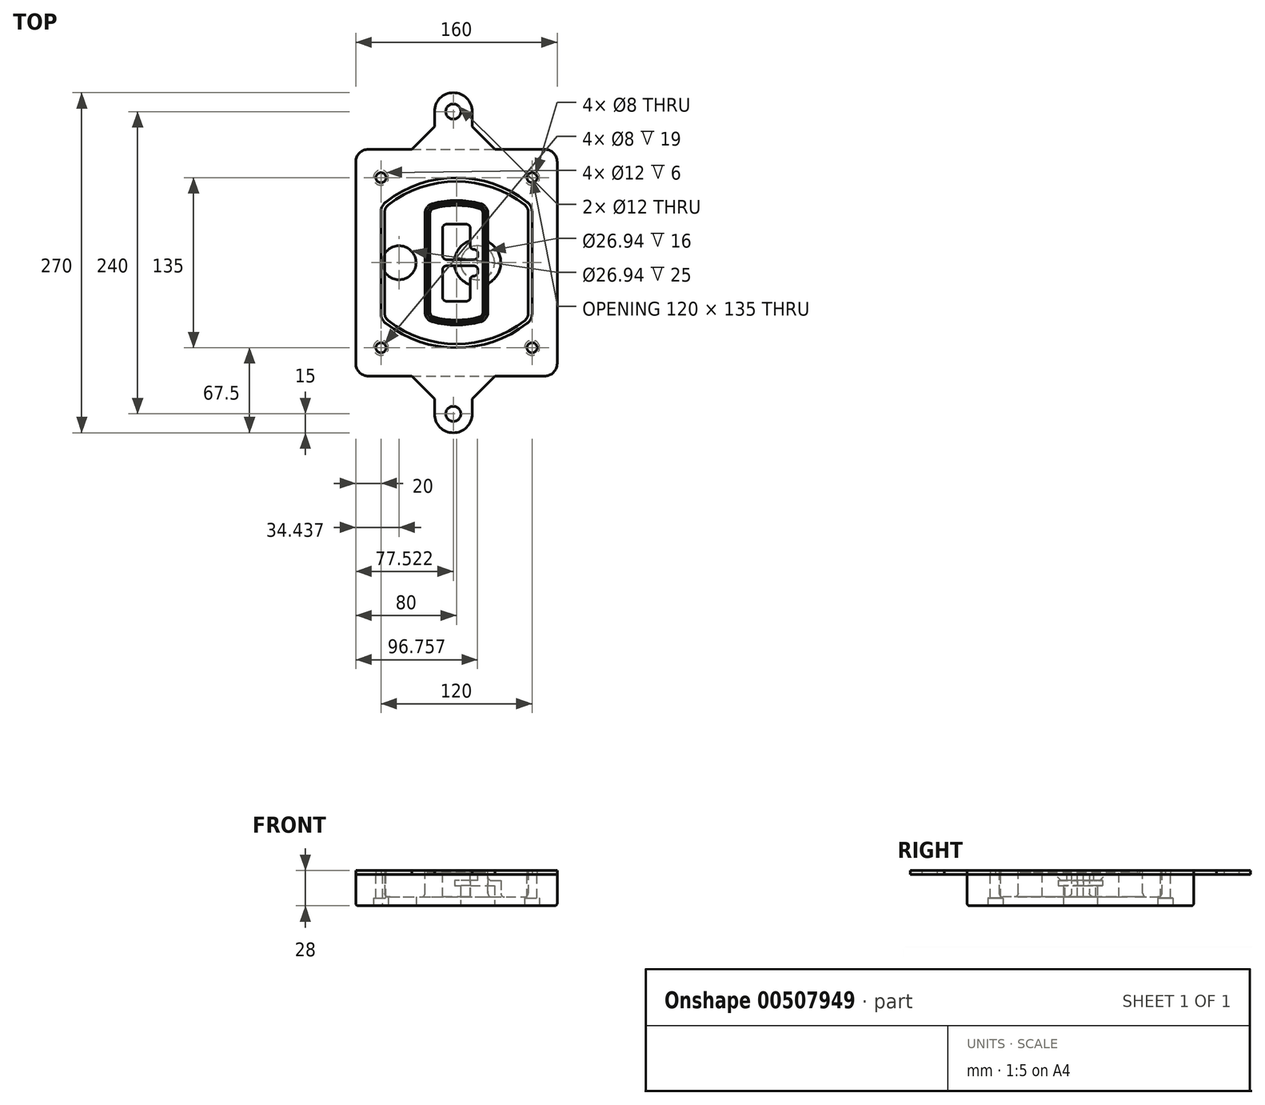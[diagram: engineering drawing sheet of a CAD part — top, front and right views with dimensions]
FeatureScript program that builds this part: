
annotation { "Feature Type Name" : "Feature", "Feature Type Description" : "" }
export const myFeature = defineFeature(function(context is Context, id is Id, definition is map)
    precondition{}
    {
        {
            var Q0;
            Q0=qCreatedBy(makeId("Top.planeOp"),FACE);
            var sketch = newSketch(context, id + "F0", { "sketchPlane" : qUnion([Q0])});
            skPoint(sketch, "E0.rect.middle", {"position": v(0, 0) * mm});
            skLineSegment(sketch, "E1.bottom", {"start": v(-70, -90) * mm, "end": v(70, -90) * mm});
            skLineSegment(sketch, "E1.top", {"start": v(-70, 90) * mm, "end": v(70, 90) * mm});
            skLineSegment(sketch, "E1.left", {"start": v(-80, -80) * mm, "end": v(-80, 80) * mm});
            skLineSegment(sketch, "E1.right", {"start": v(80, -80) * mm, "end": v(80, 80) * mm});
            skLineSegment(sketch, "E2", {"start": v(-80, 90) * mm, "end": v(80, -90) * mm, "construction": true});
            skLineSegment(sketch, "E3", {"start": v(80, 90) * mm, "end": v(-80, -90) * mm, "construction": true});
            skCircle(sketch, "E4", {"center": v(-60, 67.5) * mm, "radius": 4 * mm});
            skCircle(sketch, "E5", {"center": v(60, 67.5) * mm, "radius": 4 * mm});
            skCircle(sketch, "E6", {"center": v(60, -67.5) * mm, "radius": 4 * mm});
            skCircle(sketch, "E7", {"center": v(-60, -67.5) * mm, "radius": 4 * mm});
            skLineSegment(sketch, "E8", {"start": v(-60, 67.5) * mm, "end": v(60, 67.5) * mm, "construction": true});
            skLineSegment(sketch, "E9", {"start": v(60, 67.5) * mm, "end": v(60, -67.5) * mm, "construction": true});
            skLineSegment(sketch, "E10", {"start": v(60, -67.5) * mm, "end": v(-60, -67.5) * mm, "construction": true});
            skLineSegment(sketch, "E11", {"start": v(-60, -67.5) * mm, "end": v(-60, 67.5) * mm, "construction": true});
            skLineSegment(sketch, "E12", {"start": v(-60, 40.3) * mm, "end": v(-60, -40.3) * mm});
            skLineSegment(sketch, "E13", {"start": v(60, 40.3) * mm, "end": v(60, -40.3) * mm});
            skArc(sketch, "E14", {"start": v(56.15, 48.18) * mm, "mid": v(0, 67.5) * mm, "end": v(-56.15, 48.18) * mm});
            skArc(sketch, "E15", {"start": v(-56.15, -48.18) * mm, "mid": v(0, -67.5) * mm, "end": v(56.15, -48.18) * mm});
            skLineSegment(sketch, "E16", {"start": v(-60, 0) * mm, "end": v(60, 0) * mm, "construction": true});
            skPoint(sketch, "E17.visualSharp", {"position": v(-60, -45) * mm});
            skArc(sketch, "E17.filletArc", {"start": v(-60, -40.3) * mm, "mid": v(-58.99, -44.68) * mm, "end": v(-56.15, -48.18) * mm});
            skPoint(sketch, "E18.visualSharp", {"position": v(-60, 45) * mm});
            skArc(sketch, "E18.filletArc", {"start": v(-56.15, 48.18) * mm, "mid": v(-58.99, 44.68) * mm, "end": v(-60, 40.3) * mm});
            skPoint(sketch, "E19.visualSharp", {"position": v(60, 45) * mm});
            skArc(sketch, "E19.filletArc", {"start": v(60, 40.3) * mm, "mid": v(58.99, 44.68) * mm, "end": v(56.15, 48.18) * mm});
            skPoint(sketch, "E20.visualSharp", {"position": v(60, -45) * mm});
            skArc(sketch, "E20.filletArc", {"start": v(56.15, -48.18) * mm, "mid": v(58.99, -44.68) * mm, "end": v(60, -40.3) * mm});
            skPoint(sketch, "E21.visualSharp", {"position": v(-80, 90) * mm});
            skArc(sketch, "E21.filletArc", {"start": v(-70, 90) * mm, "mid": v(-77.07, 87.07) * mm, "end": v(-80, 80) * mm});
            skPoint(sketch, "E22.visualSharp", {"position": v(80, 90) * mm});
            skArc(sketch, "E22.filletArc", {"start": v(80, 80) * mm, "mid": v(77.07, 87.07) * mm, "end": v(70, 90) * mm});
            skPoint(sketch, "E23.visualSharp", {"position": v(80, -90) * mm});
            skArc(sketch, "E23.filletArc", {"start": v(70, -90) * mm, "mid": v(77.07, -87.07) * mm, "end": v(80, -80) * mm});
            skPoint(sketch, "E24.visualSharp", {"position": v(-80, -90) * mm});
            skArc(sketch, "E24.filletArc", {"start": v(-80, -80) * mm, "mid": v(-77.07, -87.07) * mm, "end": v(-70, -90) * mm});
            skArc(sketch, "E25.0", {"start": v(57, 40.3) * mm, "mid": v(56.3, 43.36) * mm, "end": v(54.3, 45.81) * mm});
            skLineSegment(sketch, "E25.1", {"start": v(57, 40.3) * mm, "end": v(57, -40.3) * mm});
            skArc(sketch, "E25.2", {"start": v(54.3, -45.81) * mm, "mid": v(56.3, -43.36) * mm, "end": v(57, -40.3) * mm});
            skArc(sketch, "E25.3", {"start": v(-54.3, -45.81) * mm, "mid": v(0, -64.5) * mm, "end": v(54.3, -45.81) * mm});
            skArc(sketch, "E25.4", {"start": v(-57, -40.3) * mm, "mid": v(-56.3, -43.36) * mm, "end": v(-54.3, -45.81) * mm});
            skArc(sketch, "E25.5", {"start": v(54.3, 45.81) * mm, "mid": v(0, 64.5) * mm, "end": v(-54.3, 45.81) * mm});
            skLineSegment(sketch, "E25.6", {"start": v(-57, 40.3) * mm, "end": v(-57, -40.3) * mm});
            skArc(sketch, "E25.7", {"start": v(-54.3, 45.81) * mm, "mid": v(-56.3, 43.36) * mm, "end": v(-57, 40.3) * mm});
            skArc(sketch, "E26.0", {"start": v(-58.62, 51.33) * mm, "mid": v(-62.58, 46.43) * mm, "end": v(-64, 40.3) * mm});
            skArc(sketch, "E26.1", {"start": v(58.62, 51.33) * mm, "mid": v(0, 71.5) * mm, "end": v(-58.62, 51.33) * mm});
            skArc(sketch, "E26.2", {"start": v(64, 40.3) * mm, "mid": v(62.58, 46.43) * mm, "end": v(58.62, 51.33) * mm});
            skLineSegment(sketch, "E26.3", {"start": v(64, 40.3) * mm, "end": v(64, -40.3) * mm});
            skArc(sketch, "E26.4", {"start": v(58.62, -51.33) * mm, "mid": v(62.58, -46.43) * mm, "end": v(64, -40.3) * mm});
            skLineSegment(sketch, "E26.5", {"start": v(-64, 40.3) * mm, "end": v(-64, -40.3) * mm});
            skArc(sketch, "E26.6", {"start": v(-58.62, -51.33) * mm, "mid": v(0, -71.5) * mm, "end": v(58.62, -51.33) * mm});
            skArc(sketch, "E26.7", {"start": v(-64, -40.3) * mm, "mid": v(-62.58, -46.43) * mm, "end": v(-58.62, -51.33) * mm});
            skSolve(sketch);
        }
        {
            var Q0;
            Q0=makeQuery(id+"F0.imprint","IMPRINT",FACE,{"disambiguationData":[TD([[makeQuery(id+"F0.imprint","IMPRINT",EDGE,{"derivedFrom":sQuery(id+"F0.wireOp",EDGE,"E1.bottom")}),1.0]])]});
            var Q1;
            Q1=makeQuery(id+"F0.imprint","IMPRINT",FACE,{"disambiguationData":[TD([[makeQuery(id+"F0.imprint","IMPRINT",EDGE,{"derivedFrom":sQuery(id+"F0.wireOp",EDGE,"E12")}),1.0]])]});
            var Q2;
            Q2=makeQuery(id+"F0.imprint","IMPRINT",FACE,{"disambiguationData":[TD([[makeQuery(id+"F0.imprint","IMPRINT",EDGE,{"derivedFrom":sQuery(id+"F0.wireOp",EDGE,"E25.0")}),1.0]])]});
            var Q3;
            Q3=makeQuery(id+"F0.imprint","IMPRINT",FACE,{"disambiguationData":[TD([[makeQuery(id+"F0.imprint","IMPRINT",EDGE,{"derivedFrom":sQuery(id+"F0.wireOp",EDGE,"E12")}),-1.0]])]});
            extrude(context, id + "F1", {"entities" : qUnion([Q0, Q1, Q2, Q3]), "oppositeDirection" : true, "depth" : 25 * mm});
        }
        {
            var Q0;
            Q0=makeQuery(id+"F0.imprint","IMPRINT",FACE,{"disambiguationData":[TD([[makeQuery(id+"F0.imprint","IMPRINT",EDGE,{"derivedFrom":sQuery(id+"F0.wireOp",EDGE,"E12")}),1.0]])]});
            extrude(context, id + "F2", {"entities" : qUnion([Q0]), "operationType" : NewBodyOperationType.ADD, "depth" : 3 * mm});
        }
        {
            var Q0;
            Q0=makeQuery(id+"F0.imprint","IMPRINT",FACE,{"disambiguationData":[TD([[makeQuery(id+"F0.imprint","IMPRINT",EDGE,{"derivedFrom":sQuery(id+"F0.wireOp",EDGE,"E25.0")}),1.0]])]});
            extrude(context, id + "F3", {"entities" : qUnion([Q0]), "operationType" : NewBodyOperationType.REMOVE, "oppositeDirection" : true, "depth" : 18 * mm});
        }
        {
            var Q0;
            Q0=makeQuery(id+"F2.opExtrude","CAP_FACE",FACE,{"disambiguationData":[OSD([sQuery(id+"F0.wireOp",EDGE,"E12"),sQuery(id+"F0.wireOp",EDGE,"E13"),sQuery(id+"F0.wireOp",EDGE,"E14"),sQuery(id+"F0.wireOp",EDGE,"E15"),sQuery(id+"F0.wireOp",EDGE,"E17.filletArc"),sQuery(id+"F0.wireOp",EDGE,"E18.filletArc"),sQuery(id+"F0.wireOp",EDGE,"E19.filletArc"),sQuery(id+"F0.wireOp",EDGE,"E20.filletArc"),sQuery(id+"F0.wireOp",EDGE,"E25.0"),sQuery(id+"F0.wireOp",EDGE,"E25.1"),sQuery(id+"F0.wireOp",EDGE,"E25.2"),sQuery(id+"F0.wireOp",EDGE,"E25.3"),sQuery(id+"F0.wireOp",EDGE,"E25.4"),sQuery(id+"F0.wireOp",EDGE,"E25.5"),sQuery(id+"F0.wireOp",EDGE,"E25.6"),sQuery(id+"F0.wireOp",EDGE,"E25.7")])],"isStart":false});
            var sketch = newSketch(context, id + "F4", { "sketchPlane" : qUnion([Q0])});
            skArc(sketch, "E27.0", {"start": v(-19.08, -46.97) * mm, "mid": v(0, -49.5) * mm, "end": v(19.08, -46.97) * mm});
            skArc(sketch, "E28.0", {"start": v(19.08, 46.97) * mm, "mid": v(0, 49.5) * mm, "end": v(-19.08, 46.97) * mm});
            skLineSegment(sketch, "E29", {"start": v(-25, 39.25) * mm, "end": v(-25, -39.25) * mm});
            skLineSegment(sketch, "E30", {"start": v(25, 39.25) * mm, "end": v(25, -39.25) * mm});
            skLineSegment(sketch, "E31", {"start": v(-25, 45.1) * mm, "end": v(25, 45.1) * mm, "construction": true});
            skLineSegment(sketch, "E32", {"start": v(-25, -45.1) * mm, "end": v(25, -45.1) * mm, "construction": true});
            skPoint(sketch, "E33.visualSharp", {"position": v(-25, 45.1) * mm});
            skArc(sketch, "E33.filletArc", {"start": v(-19.08, 46.97) * mm, "mid": v(-23.35, 44.11) * mm, "end": v(-25, 39.25) * mm});
            skPoint(sketch, "E34.visualSharp", {"position": v(25, 45.1) * mm});
            skArc(sketch, "E34.filletArc", {"start": v(25, 39.25) * mm, "mid": v(23.35, 44.11) * mm, "end": v(19.08, 46.97) * mm});
            skPoint(sketch, "E35.visualSharp", {"position": v(25, -45.1) * mm});
            skArc(sketch, "E35.filletArc", {"start": v(19.08, -46.97) * mm, "mid": v(23.35, -44.11) * mm, "end": v(25, -39.25) * mm});
            skPoint(sketch, "E36.visualSharp", {"position": v(-25, -45.1) * mm});
            skArc(sketch, "E36.filletArc", {"start": v(-25, -39.25) * mm, "mid": v(-23.35, -44.11) * mm, "end": v(-19.08, -46.97) * mm});
            skArc(sketch, "E37.0", {"start": v(54.3, 45.81) * mm, "mid": v(0, 64.5) * mm, "end": v(-54.3, 45.81) * mm});
            skArc(sketch, "E37.1", {"start": v(-54.3, 45.81) * mm, "mid": v(-56.3, 43.36) * mm, "end": v(-57, 40.3) * mm});
            skLineSegment(sketch, "E37.2", {"start": v(-57, 40.3) * mm, "end": v(-57, -40.3) * mm});
            skArc(sketch, "E37.3", {"start": v(-57, -40.3) * mm, "mid": v(-56.3, -43.36) * mm, "end": v(-54.3, -45.81) * mm});
            skArc(sketch, "E37.4", {"start": v(-54.3, -45.81) * mm, "mid": v(0, -64.5) * mm, "end": v(54.3, -45.81) * mm});
            skArc(sketch, "E37.5", {"start": v(54.3, -45.81) * mm, "mid": v(56.3, -43.36) * mm, "end": v(57, -40.3) * mm});
            skLineSegment(sketch, "E37.6", {"start": v(57, 40.3) * mm, "end": v(57, -40.3) * mm});
            skArc(sketch, "E37.7", {"start": v(57, 40.3) * mm, "mid": v(56.3, 43.36) * mm, "end": v(54.3, 45.81) * mm});
            skLineSegment(sketch, "E38.0", {"start": v(23, 39.25) * mm, "end": v(23, -39.25) * mm});
            skArc(sketch, "E38.1", {"start": v(18.56, -45.04) * mm, "mid": v(21.76, -42.9) * mm, "end": v(23, -39.25) * mm});
            skArc(sketch, "E38.2", {"start": v(-18.56, -45.04) * mm, "mid": v(0, -47.5) * mm, "end": v(18.56, -45.04) * mm});
            skArc(sketch, "E38.3", {"start": v(-23, -39.25) * mm, "mid": v(-21.76, -42.9) * mm, "end": v(-18.56, -45.04) * mm});
            skLineSegment(sketch, "E38.4", {"start": v(-23, 39.25) * mm, "end": v(-23, -39.25) * mm});
            skArc(sketch, "E38.5", {"start": v(23, 39.25) * mm, "mid": v(21.76, 42.9) * mm, "end": v(18.56, 45.04) * mm});
            skArc(sketch, "E38.6", {"start": v(-18.56, 45.04) * mm, "mid": v(-21.76, 42.9) * mm, "end": v(-23, 39.25) * mm});
            skArc(sketch, "E38.7", {"start": v(18.56, 45.04) * mm, "mid": v(0, 47.5) * mm, "end": v(-18.56, 45.04) * mm});
            skArc(sketch, "E39.0", {"start": v(21, 39.25) * mm, "mid": v(20.18, 41.68) * mm, "end": v(18.04, 43.1) * mm});
            skLineSegment(sketch, "E39.1", {"start": v(21, 39.25) * mm, "end": v(21, -39.25) * mm});
            skArc(sketch, "E39.2", {"start": v(18.04, -43.1) * mm, "mid": v(20.18, -41.68) * mm, "end": v(21, -39.25) * mm});
            skArc(sketch, "E39.3", {"start": v(-18.04, -43.1) * mm, "mid": v(0, -45.5) * mm, "end": v(18.04, -43.1) * mm});
            skArc(sketch, "E39.4", {"start": v(-21, -39.25) * mm, "mid": v(-20.18, -41.68) * mm, "end": v(-18.04, -43.1) * mm});
            skArc(sketch, "E39.5", {"start": v(18.04, 43.1) * mm, "mid": v(0, 45.5) * mm, "end": v(-18.04, 43.1) * mm});
            skLineSegment(sketch, "E39.6", {"start": v(-21, 39.25) * mm, "end": v(-21, -39.25) * mm});
            skArc(sketch, "E39.7", {"start": v(-18.04, 43.1) * mm, "mid": v(-20.18, 41.68) * mm, "end": v(-21, 39.25) * mm});
            skLineSegment(sketch, "E40", {"start": v(-25, 0) * mm, "end": v(25, 0) * mm, "construction": true});
            skLineSegment(sketch, "E41", {"start": v(-11, 5.5) * mm, "end": v(-11, 27.5) * mm});
            skLineSegment(sketch, "E42", {"start": v(-8, 30.5) * mm, "end": v(8, 30.5) * mm});
            skLineSegment(sketch, "E43", {"start": v(11, 27.5) * mm, "end": v(11, 13.5) * mm});
            skLineSegment(sketch, "E44", {"start": v(14, 10.5) * mm, "end": v(14, 10.5) * mm});
            skLineSegment(sketch, "E45", {"start": v(17, 7.5) * mm, "end": v(17, 5.5) * mm});
            skLineSegment(sketch, "E46", {"start": v(14, 2.5) * mm, "end": v(-8, 2.5) * mm});
            skPoint(sketch, "E47.visualSharp", {"position": v(-11, 30.5) * mm});
            skArc(sketch, "E47.filletArc", {"start": v(-8, 30.5) * mm, "mid": v(-10.12, 29.62) * mm, "end": v(-11, 27.5) * mm});
            skPoint(sketch, "E48.visualSharp", {"position": v(11, 30.5) * mm});
            skArc(sketch, "E48.filletArc", {"start": v(11, 27.5) * mm, "mid": v(10.12, 29.62) * mm, "end": v(8, 30.5) * mm});
            skPoint(sketch, "E49.visualSharp", {"position": v(11, 10.5) * mm});
            skArc(sketch, "E49.filletArc", {"start": v(11, 13.5) * mm, "mid": v(11.88, 11.38) * mm, "end": v(14, 10.5) * mm});
            skPoint(sketch, "E50.visualSharp", {"position": v(17, 10.5) * mm});
            skArc(sketch, "E50.filletArc", {"start": v(17, 7.5) * mm, "mid": v(16.12, 9.62) * mm, "end": v(14, 10.5) * mm});
            skPoint(sketch, "E51.visualSharp", {"position": v(17, 2.5) * mm});
            skArc(sketch, "E51.filletArc", {"start": v(14, 2.5) * mm, "mid": v(16.12, 3.38) * mm, "end": v(17, 5.5) * mm});
            skPoint(sketch, "E52.visualSharp", {"position": v(-11, 2.5) * mm});
            skArc(sketch, "E52.filletArc", {"start": v(-11, 5.5) * mm, "mid": v(-10.12, 3.38) * mm, "end": v(-8, 2.5) * mm});
            skLineSegment(sketch, "E53.0.MirrorCS", {"start": v(14, -2.5) * mm, "end": v(-8, -2.5) * mm});
            skArc(sketch, "E54.0.MirrorCS", {"start": v(-11, -5.5) * mm, "mid": v(-10.12, -3.38) * mm, "end": v(-8, -2.5) * mm});
            skLineSegment(sketch, "E55.0.MirrorCS", {"start": v(-11, -5.5) * mm, "end": v(-11, -27.5) * mm});
            skArc(sketch, "E56.0.MirrorCS", {"start": v(-8, -30.5) * mm, "mid": v(-10.12, -29.62) * mm, "end": v(-11, -27.5) * mm});
            skLineSegment(sketch, "E57.0.MirrorCS", {"start": v(-8, -30.5) * mm, "end": v(8, -30.5) * mm});
            skArc(sketch, "E58.0.MirrorCS", {"start": v(11, -27.5) * mm, "mid": v(10.12, -29.62) * mm, "end": v(8, -30.5) * mm});
            skLineSegment(sketch, "E59.0.MirrorCS", {"start": v(11, -27.5) * mm, "end": v(11, -13.5) * mm});
            skArc(sketch, "E60.0.MirrorCS", {"start": v(11, -13.5) * mm, "mid": v(11.88, -11.38) * mm, "end": v(14, -10.5) * mm});
            skArc(sketch, "E61.0.MirrorCS", {"start": v(17, -7.5) * mm, "mid": v(16.12, -9.62) * mm, "end": v(14, -10.5) * mm});
            skLineSegment(sketch, "E62.0.MirrorCS", {"start": v(17, -7.5) * mm, "end": v(17, -5.5) * mm});
            skArc(sketch, "E63.0.MirrorCS", {"start": v(14, -2.5) * mm, "mid": v(16.12, -3.38) * mm, "end": v(17, -5.5) * mm});
            skSolve(sketch);
        }
        {
            var Q0;
            Q0=makeQuery(id+"F4.imprint","IMPRINT",FACE,{"disambiguationData":[TD([[makeQuery(id+"F4.imprint","IMPRINT",EDGE,{"derivedFrom":sQuery(id+"F4.wireOp",EDGE,"E27.0")}),1.0]])]});
            var Q1;
            Q1=makeQuery(id+"F4.imprint","IMPRINT",FACE,{"disambiguationData":[TD([[makeQuery(id+"F4.imprint","IMPRINT",EDGE,{"derivedFrom":sQuery(id+"F4.wireOp",EDGE,"E38.0")}),-1.0]])]});
            var Q2;
            Q2=makeQuery(id+"F4.imprint","IMPRINT",FACE,{"disambiguationData":[TD([[makeQuery(id+"F4.imprint","IMPRINT",EDGE,{"derivedFrom":sQuery(id+"F4.wireOp",EDGE,"E39.0")}),1.0]])]});
            extrude(context, id + "F5", {"entities" : qUnion([Q0, Q1, Q2]), "operationType" : NewBodyOperationType.ADD, "endBound" : BoundingType.UP_TO_NEXT, "oppositeDirection" : true, "depth" : 25 * mm});
        }
        {
            var Q0;
            Q0=makeQuery(id+"F4.imprint","IMPRINT",FACE,{"disambiguationData":[TD([[makeQuery(id+"F4.imprint","IMPRINT",EDGE,{"derivedFrom":sQuery(id+"F4.wireOp",EDGE,"E38.0")}),-1.0]])]});
            extrude(context, id + "F6", {"entities" : qUnion([Q0]), "operationType" : NewBodyOperationType.REMOVE, "oppositeDirection" : true, "depth" : 2 * mm});
        }
        {
            var Q0;
            Q0=makeQuery(id+"F1.opExtrude","CAP_FACE",FACE,{"disambiguationData":[OSD([sQuery(id+"F0.wireOp",EDGE,"E1.bottom"),sQuery(id+"F0.wireOp",EDGE,"E1.top"),sQuery(id+"F0.wireOp",EDGE,"E1.left"),sQuery(id+"F0.wireOp",EDGE,"E1.right"),sQuery(id+"F0.wireOp",EDGE,"E4"),sQuery(id+"F0.wireOp",EDGE,"E5"),sQuery(id+"F0.wireOp",EDGE,"E6"),sQuery(id+"F0.wireOp",EDGE,"E7"),sQuery(id+"F0.wireOp",EDGE,"E21.filletArc"),sQuery(id+"F0.wireOp",EDGE,"E22.filletArc"),sQuery(id+"F0.wireOp",EDGE,"E23.filletArc"),sQuery(id+"F0.wireOp",EDGE,"E24.filletArc")])],"isStart":false});
            var sketch = newSketch(context, id + "F7", { "sketchPlane" : qUnion([Q0])});
            skCircle(sketch, "E64", {"center": v(16.76, 0) * mm, "radius": 13.47 * mm});
            skCircle(sketch, "E65", {"center": v(-45.56, 0) * mm, "radius": 13.47 * mm});
            skLineSegment(sketch, "E66", {"start": v(80, 0) * mm, "end": v(-80, 0) * mm});
            skCircle(sketch, "E67", {"center": v(16.76, 0) * mm, "radius": 18.47 * mm});
            skCircle(sketch, "E68", {"center": v(60, -67.5) * mm, "radius": 6 * mm});
            skCircle(sketch, "E69", {"center": v(-60, -67.5) * mm, "radius": 6 * mm});
            skCircle(sketch, "E70", {"center": v(-60, 67.5) * mm, "radius": 6 * mm});
            skCircle(sketch, "E71", {"center": v(60, 67.5) * mm, "radius": 6 * mm});
            skSolve(sketch);
        }
        {
            var Q0;
            {var subQ1=sQuery(id+"F7.wireOp",EDGE,"E66");var subQ4=sQuery(id+"F7.wireOp",EDGE,"E64");var subQ6=makeQuery(id+"F7.imprint","INTERSECT",VERTEX,{"disambiguationData":[OD(0.0)],"derivedFrom":[subQ4,subQ1]});Q0=makeQuery(id+"F7.imprint","IMPRINT",FACE,{"disambiguationData":[TD([[makeQuery(id+"F7.imprint","IMPRINT",EDGE,{"disambiguationData":[TD([[subQ6,-1.0]])],"derivedFrom":subQ4}),-1.0]])]});}
            var Q1;
            {var subQ0=sQuery(id+"F7.wireOp",EDGE,"E66");var subQ1=sQuery(id+"F7.wireOp",EDGE,"E64");var subQ3=makeQuery(id+"F7.imprint","INTERSECT",VERTEX,{"disambiguationData":[OD(0.0)],"derivedFrom":[subQ1,subQ0]});Q1=makeQuery(id+"F7.imprint","IMPRINT",FACE,{"disambiguationData":[TD([[makeQuery(id+"F7.imprint","IMPRINT",EDGE,{"disambiguationData":[TD([[subQ3,-1.0]])],"derivedFrom":subQ1}),1.0]])]});}
            var Q2;
            {var subQ0=sQuery(id+"F7.wireOp",EDGE,"E66");var subQ1=sQuery(id+"F7.wireOp",EDGE,"E64");var subQ3=makeQuery(id+"F7.imprint","INTERSECT",VERTEX,{"disambiguationData":[OD(0.0)],"derivedFrom":[subQ1,subQ0]});Q2=makeQuery(id+"F7.imprint","IMPRINT",FACE,{"disambiguationData":[TD([[makeQuery(id+"F7.imprint","IMPRINT",EDGE,{"disambiguationData":[TD([[subQ3,1.0]])],"derivedFrom":subQ1}),1.0]])]});}
            var Q3;
            {var subQ1=sQuery(id+"F7.wireOp",EDGE,"E66");var subQ4=sQuery(id+"F7.wireOp",EDGE,"E64");var subQ6=makeQuery(id+"F7.imprint","INTERSECT",VERTEX,{"disambiguationData":[OD(0.0)],"derivedFrom":[subQ4,subQ1]});Q3=makeQuery(id+"F7.imprint","IMPRINT",FACE,{"disambiguationData":[TD([[makeQuery(id+"F7.imprint","IMPRINT",EDGE,{"disambiguationData":[TD([[subQ6,1.0]])],"derivedFrom":subQ4}),-1.0]])]});}
            extrude(context, id + "F8", {"entities" : qUnion([Q0, Q1, Q2, Q3]), "operationType" : NewBodyOperationType.ADD, "oppositeDirection" : true, "depth" : 20 * mm});
        }
        {
            var Q0;
            {var subQ0=sQuery(id+"F7.wireOp",EDGE,"E66");var subQ1=sQuery(id+"F7.wireOp",EDGE,"E64");var subQ3=makeQuery(id+"F7.imprint","INTERSECT",VERTEX,{"disambiguationData":[OD(0.0)],"derivedFrom":[subQ1,subQ0]});Q0=makeQuery(id+"F7.imprint","IMPRINT",FACE,{"disambiguationData":[TD([[makeQuery(id+"F7.imprint","IMPRINT",EDGE,{"disambiguationData":[TD([[subQ3,-1.0]])],"derivedFrom":subQ1}),1.0]])]});}
            var Q1;
            {var subQ0=sQuery(id+"F7.wireOp",EDGE,"E66");var subQ1=sQuery(id+"F7.wireOp",EDGE,"E64");var subQ3=makeQuery(id+"F7.imprint","INTERSECT",VERTEX,{"disambiguationData":[OD(0.0)],"derivedFrom":[subQ1,subQ0]});Q1=makeQuery(id+"F7.imprint","IMPRINT",FACE,{"disambiguationData":[TD([[makeQuery(id+"F7.imprint","IMPRINT",EDGE,{"disambiguationData":[TD([[subQ3,1.0]])],"derivedFrom":subQ1}),1.0]])]});}
            extrude(context, id + "F9", {"entities" : qUnion([Q0, Q1]), "operationType" : NewBodyOperationType.REMOVE, "oppositeDirection" : true, "depth" : 16 * mm});
        }
        {
            var Q0;
            {var subQ0=sQuery(id+"F7.wireOp",EDGE,"E66");var subQ1=sQuery(id+"F7.wireOp",EDGE,"E65");var subQ3=makeQuery(id+"F7.imprint","INTERSECT",VERTEX,{"disambiguationData":[OD(0.0)],"derivedFrom":[subQ1,subQ0]});Q0=makeQuery(id+"F7.imprint","IMPRINT",FACE,{"disambiguationData":[TD([[makeQuery(id+"F7.imprint","IMPRINT",EDGE,{"disambiguationData":[TD([[subQ3,-1.0]])],"derivedFrom":subQ1}),1.0]])]});}
            var Q1;
            {var subQ0=sQuery(id+"F7.wireOp",EDGE,"E66");var subQ1=sQuery(id+"F7.wireOp",EDGE,"E65");var subQ3=makeQuery(id+"F7.imprint","INTERSECT",VERTEX,{"disambiguationData":[OD(0.0)],"derivedFrom":[subQ1,subQ0]});Q1=makeQuery(id+"F7.imprint","IMPRINT",FACE,{"disambiguationData":[TD([[makeQuery(id+"F7.imprint","IMPRINT",EDGE,{"disambiguationData":[TD([[subQ3,1.0]])],"derivedFrom":subQ1}),1.0]])]});}
            extrude(context, id + "F10", {"entities" : qUnion([Q0, Q1]), "operationType" : NewBodyOperationType.REMOVE, "oppositeDirection" : true, "depth" : 25 * mm});
        }
        {
            var Q0;
            Q0=makeQuery(id+"F7.imprint","IMPRINT",FACE,{"disambiguationData":[TD([[makeQuery(id+"F7.imprint","IMPRINT",EDGE,{"derivedFrom":sQuery(id+"F7.wireOp",EDGE,"E68")}),1.0]])]});
            var Q1;
            Q1=makeQuery(id+"F7.imprint","IMPRINT",FACE,{"disambiguationData":[TD([[makeQuery(id+"F7.imprint","IMPRINT",EDGE,{"derivedFrom":makeQuery(id+"F1.opExtrude","CAP_EDGE",EDGE,{"disambiguationData":[OSD([sQuery(id+"F0.wireOp",EDGE,"E5")])],"isStart":false})}),-1.0]])]});
            var Q2;
            Q2=makeQuery(id+"F7.imprint","IMPRINT",FACE,{"disambiguationData":[TD([[makeQuery(id+"F7.imprint","IMPRINT",EDGE,{"derivedFrom":sQuery(id+"F7.wireOp",EDGE,"E69")}),1.0]])]});
            var Q3;
            Q3=makeQuery(id+"F7.imprint","IMPRINT",FACE,{"disambiguationData":[TD([[makeQuery(id+"F7.imprint","IMPRINT",EDGE,{"derivedFrom":makeQuery(id+"F1.opExtrude","CAP_EDGE",EDGE,{"disambiguationData":[OSD([sQuery(id+"F0.wireOp",EDGE,"E4")])],"isStart":false})}),-1.0]])]});
            var Q4;
            Q4=makeQuery(id+"F7.imprint","IMPRINT",FACE,{"disambiguationData":[TD([[makeQuery(id+"F7.imprint","IMPRINT",EDGE,{"derivedFrom":sQuery(id+"F7.wireOp",EDGE,"E70")}),1.0]])]});
            var Q5;
            Q5=makeQuery(id+"F7.imprint","IMPRINT",FACE,{"disambiguationData":[TD([[makeQuery(id+"F7.imprint","IMPRINT",EDGE,{"derivedFrom":makeQuery(id+"F1.opExtrude","CAP_EDGE",EDGE,{"disambiguationData":[OSD([sQuery(id+"F0.wireOp",EDGE,"E7")])],"isStart":false})}),-1.0]])]});
            var Q6;
            Q6=makeQuery(id+"F7.imprint","IMPRINT",FACE,{"disambiguationData":[TD([[makeQuery(id+"F7.imprint","IMPRINT",EDGE,{"derivedFrom":sQuery(id+"F7.wireOp",EDGE,"E71")}),1.0]])]});
            var Q7;
            Q7=makeQuery(id+"F7.imprint","IMPRINT",FACE,{"disambiguationData":[TD([[makeQuery(id+"F7.imprint","IMPRINT",EDGE,{"derivedFrom":makeQuery(id+"F1.opExtrude","CAP_EDGE",EDGE,{"disambiguationData":[OSD([sQuery(id+"F0.wireOp",EDGE,"E6")])],"isStart":false})}),-1.0]])]});
            extrude(context, id + "F11", {"entities" : qUnion([Q0, Q1, Q2, Q3, Q4, Q5, Q6, Q7]), "operationType" : NewBodyOperationType.REMOVE, "oppositeDirection" : true, "depth" : 6 * mm});
        }
        {
            var Q0;
            Q0=makeQuery(id+"F9.boolean.opBoolean","COPY",FACE,{"derivedFrom":makeQuery(id+"F9.opExtrude","CAP_FACE",FACE,{"disambiguationData":[OSD([sQuery(id+"F7.wireOp",EDGE,"E64")])],"isStart":false})});
            var sketch = newSketch(context, id + "F12", { "sketchPlane" : qUnion([Q0])});
            skArc(sketch, "E72.0", {"start": v(11, 17.55) * mm, "mid": v(2.57, 11.82) * mm, "end": v(-1.54, 2.5) * mm});
            skArc(sketch, "E72.1", {"start": v(-1.54, -2.5) * mm, "mid": v(2.57, -11.82) * mm, "end": v(11, -17.55) * mm});
            skLineSegment(sketch, "E73", {"start": v(-1.54, -2.5) * mm, "end": v(14, -2.5) * mm});
            skLineSegment(sketch, "E74.0", {"start": v(14, 2.5) * mm, "end": v(-1.54, 2.5) * mm});
            skArc(sketch, "E74.1", {"start": v(14, 2.5) * mm, "mid": v(16.12, 3.38) * mm, "end": v(17, 5.5) * mm});
            skLineSegment(sketch, "E74.2", {"start": v(17, 7.5) * mm, "end": v(17, 5.5) * mm});
            skArc(sketch, "E74.3", {"start": v(17, 7.5) * mm, "mid": v(16.12, 9.62) * mm, "end": v(14, 10.5) * mm});
            skArc(sketch, "E74.4", {"start": v(11, 13.5) * mm, "mid": v(11.88, 11.38) * mm, "end": v(14, 10.5) * mm});
            skLineSegment(sketch, "E74.5", {"start": v(11, 17.55) * mm, "end": v(11, 13.5) * mm});
            skLineSegment(sketch, "E74.7", {"start": v(14, -2.5) * mm, "end": v(-1.54, -2.5) * mm});
            skArc(sketch, "E74.8", {"start": v(14, -2.5) * mm, "mid": v(16.12, -3.38) * mm, "end": v(17, -5.5) * mm});
            skLineSegment(sketch, "E74.9", {"start": v(17, -7.5) * mm, "end": v(17, -5.5) * mm});
            skArc(sketch, "E74.10", {"start": v(17, -7.5) * mm, "mid": v(16.12, -9.62) * mm, "end": v(14, -10.5) * mm});
            skArc(sketch, "E74.11", {"start": v(11, -13.5) * mm, "mid": v(11.88, -11.38) * mm, "end": v(14, -10.5) * mm});
            skLineSegment(sketch, "E74.12", {"start": v(11, -17.55) * mm, "end": v(11, -13.5) * mm});
            skPoint(sketch, "E75.orphan", {"position": v(11, -27.5) * mm});
            skPoint(sketch, "E76.orphan", {"position": v(-8, -2.5) * mm});
            skPoint(sketch, "E77.orphan", {"position": v(-8, 2.5) * mm});
            skPoint(sketch, "E78.orphan", {"position": v(11, 27.5) * mm});
            skSolve(sketch);
        }
        {
            var Q0;
            {var subQ7=sQuery(id+"F12.wireOp",EDGE,"E72.0");var subQ14=sQuery(id+"F12.wireOp",EDGE,"E72.1");var subQ16=sQuery(id+"F12.wireOp",EDGE,"E74.1");var subQ18=sQuery(id+"F12.wireOp",EDGE,"E74.8");Q0=qUnion([makeQuery(id+"F12.imprint","IMPRINT",FACE,{"disambiguationData":[TD([[makeQuery(id+"F12.imprint","IMPRINT",EDGE,{"derivedFrom":subQ7}),1.0]])]}),makeQuery(id+"F12.imprint","IMPRINT",FACE,{"disambiguationData":[TD([[makeQuery(id+"F12.imprint","IMPRINT",EDGE,{"derivedFrom":subQ14}),1.0]])]}),makeQuery(id+"F12.imprint","IMPRINT",FACE,{"disambiguationData":[TD([[makeQuery(id+"F12.imprint","IMPRINT",EDGE,{"derivedFrom":subQ16}),1.0]])]}),makeQuery(id+"F12.imprint","IMPRINT",FACE,{"disambiguationData":[TD([[makeQuery(id+"F12.imprint","IMPRINT",EDGE,{"derivedFrom":subQ18}),-1.0]])]})]);}
            var Q1;
            Q1=makeQuery(id+"F5.boolean.opBoolean","SPLIT",FACE,{"disambiguationData":[TD([makeQuery(id+"F5.opExtrude","SWEPT_FACE",FACE,{"disambiguationData":[OSD([sQuery(id+"F4.wireOp",EDGE,"E41")])]})])],"derivedFrom":makeQuery(id+"F3.boolean.opBoolean","COPY",FACE,{"derivedFrom":makeQuery(id+"F3.opExtrude","CAP_FACE",FACE,{"disambiguationData":[OSD([sQuery(id+"F0.wireOp",EDGE,"E25.0"),sQuery(id+"F0.wireOp",EDGE,"E25.1"),sQuery(id+"F0.wireOp",EDGE,"E25.2"),sQuery(id+"F0.wireOp",EDGE,"E25.3"),sQuery(id+"F0.wireOp",EDGE,"E25.4"),sQuery(id+"F0.wireOp",EDGE,"E25.5"),sQuery(id+"F0.wireOp",EDGE,"E25.6"),sQuery(id+"F0.wireOp",EDGE,"E25.7")])],"isStart":false})})});
            extrude(context, id + "F13", {"entities" : qUnion([Q0]), "operationType" : NewBodyOperationType.REMOVE, "endBound" : BoundingType.UP_TO_SURFACE, "endBoundEntityFace" : qUnion([Q1]), "depth" : 25 * mm});
        }
        {
            var Q0;
            Q0=makeQuery(id+"F3.boolean.opBoolean","COPY",EDGE,{"derivedFrom":makeQuery(id+"F3.opExtrude","CAP_EDGE",EDGE,{"disambiguationData":[OSD([sQuery(id+"F0.wireOp",EDGE,"E25.6")])],"isStart":false})});
            var Q1;
            Q1=makeQuery(id+"F8.boolean.opBoolean","INTERSECT",EDGE,{"derivedFrom":[makeQuery(id+"F5.opExtrude","SWEPT_FACE",FACE,{"disambiguationData":[OSD([sQuery(id+"F4.wireOp",EDGE,"E30")])]}),makeQuery(id+"F8.opExtrude","CAP_FACE",FACE,{"disambiguationData":[OSD([sQuery(id+"F7.wireOp",EDGE,"E67")])],"isStart":false})]});
            var Q2;
            Q2=makeQuery(id+"F8.boolean.opBoolean","INTERSECT",EDGE,{"disambiguationData":[OD(1.0)],"derivedFrom":[makeQuery(id+"F5.opExtrude","SWEPT_FACE",FACE,{"disambiguationData":[OSD([sQuery(id+"F4.wireOp",EDGE,"E30")])]}),makeQuery(id+"F8.opExtrude","SWEPT_FACE",FACE,{"disambiguationData":[OSD([sQuery(id+"F7.wireOp",EDGE,"E67")])]})]});
            var Q3;
            {var subQ0=sQuery(id+"F4.wireOp",EDGE,"E30");Q3=makeQuery(id+"F8.boolean.opBoolean","SPLIT",EDGE,{"disambiguationData":[TD([makeQuery(id+"F5.opExtrude","SWEPT_FACE",FACE,{"disambiguationData":[OSD([sQuery(id+"F4.wireOp",EDGE,"E35.filletArc")])]})])],"derivedFrom":makeQuery(id+"F5.opExtrude","CAP_EDGE",EDGE,{"disambiguationData":[OSD([subQ0])],"isStart":false})});}
            var Q4;
            {var subQ0=sQuery(id+"F0.wireOp",EDGE,"E25.7");var subQ1=sQuery(id+"F0.wireOp",EDGE,"E25.1");var subQ2=sQuery(id+"F0.wireOp",EDGE,"E25.6");var subQ3=sQuery(id+"F0.wireOp",EDGE,"E25.5");var subQ4=sQuery(id+"F0.wireOp",EDGE,"E25.4");var subQ5=sQuery(id+"F0.wireOp",EDGE,"E25.0");var subQ6=sQuery(id+"F0.wireOp",EDGE,"E25.2");var subQ7=sQuery(id+"F0.wireOp",EDGE,"E25.3");Q4=makeQuery(id+"F8.boolean.opBoolean","INTERSECT",EDGE,{"derivedFrom":[makeQuery(id+"F5.boolean.opBoolean","SPLIT",FACE,{"disambiguationData":[TD([makeQuery(id+"F2.opExtrude","SWEPT_FACE",FACE,{"disambiguationData":[OSD([subQ5])]})])],"derivedFrom":makeQuery(id+"F3.boolean.opBoolean","COPY",FACE,{"derivedFrom":makeQuery(id+"F3.opExtrude","CAP_FACE",FACE,{"disambiguationData":[OSD([subQ5,subQ1,subQ6,subQ7,subQ4,subQ3,subQ2,subQ0])],"isStart":false})})}),makeQuery(id+"F8.opExtrude","SWEPT_FACE",FACE,{"disambiguationData":[OSD([sQuery(id+"F7.wireOp",EDGE,"E67")])]})]});}
            var Q5;
            Q5=makeQuery(id+"F8.boolean.opBoolean","INTERSECT",EDGE,{"disambiguationData":[OD(0.0)],"derivedFrom":[makeQuery(id+"F5.opExtrude","SWEPT_FACE",FACE,{"disambiguationData":[OSD([sQuery(id+"F4.wireOp",EDGE,"E30")])]}),makeQuery(id+"F8.opExtrude","SWEPT_FACE",FACE,{"disambiguationData":[OSD([sQuery(id+"F7.wireOp",EDGE,"E67")])]})]});
            fillet(context, id + "F14", {"entities" : qUnion([Q0, Q1, Q2, Q3, Q4, Q5]), "radius" : 3 * mm, "tangentPropagation" : true, "allowEdgeOverflow" : false});
        }
        {
            var Q0;
            Q0=makeQuery(id+"F1.opExtrude","CAP_EDGE",EDGE,{"disambiguationData":[OSD([sQuery(id+"F0.wireOp",EDGE,"E1.bottom")])],"isStart":false});
            fillet(context, id + "F15", {"entities" : qUnion([Q0]), "radius" : 2 * mm, "tangentPropagation" : true, "allowEdgeOverflow" : false});
        }
        {
            var Q0;
            {var subQ0=sQuery(id+"F0.wireOp",EDGE,"E21.filletArc");var subQ1=sQuery(id+"F0.wireOp",EDGE,"E7");var subQ2=sQuery(id+"F0.wireOp",EDGE,"E6");var subQ3=sQuery(id+"F0.wireOp",EDGE,"E5");var subQ4=sQuery(id+"F0.wireOp",EDGE,"E4");var subQ5=sQuery(id+"F0.wireOp",EDGE,"E22.filletArc");var subQ6=sQuery(id+"F0.wireOp",EDGE,"E1.bottom");var subQ7=sQuery(id+"F0.wireOp",EDGE,"E1.right");var subQ8=sQuery(id+"F0.wireOp",EDGE,"E1.top");var subQ9=sQuery(id+"F0.wireOp",EDGE,"E1.left");var subQ10=sQuery(id+"F0.wireOp",EDGE,"E23.filletArc");var subQ11=sQuery(id+"F0.wireOp",EDGE,"E24.filletArc");Q0=makeQuery(id+"F2.boolean.opBoolean","SPLIT",FACE,{"disambiguationData":[TD([makeQuery(id+"F1.opExtrude","SWEPT_FACE",FACE,{"disambiguationData":[OSD([subQ6])]})])],"derivedFrom":makeQuery(id+"F1.opExtrude","CAP_FACE",FACE,{"disambiguationData":[OSD([subQ6,subQ8,subQ9,subQ7,subQ4,subQ3,subQ2,subQ1,subQ0,subQ5,subQ10,subQ11])],"isStart":true})});}
            var sketch = newSketch(context, id + "F16", { "sketchPlane" : qUnion([Q0])});
            skArc(sketch, "E79.0", {"start": v(-70, 90) * mm, "mid": v(-77.07, 87.07) * mm, "end": v(-80, 80) * mm});
            skLineSegment(sketch, "E79.1", {"start": v(-70, 90) * mm, "end": v(70, 90) * mm});
            skArc(sketch, "E79.2", {"start": v(80, 80) * mm, "mid": v(77.07, 87.07) * mm, "end": v(70, 90) * mm});
            skCircle(sketch, "E79.3", {"center": v(60, 67.5) * mm, "radius": 4 * mm});
            skCircle(sketch, "E79.4", {"center": v(-60, 67.5) * mm, "radius": 4 * mm});
            skLineSegment(sketch, "E79.5", {"start": v(80, -80) * mm, "end": v(80, 80) * mm});
            skLineSegment(sketch, "E79.6", {"start": v(-80, -80) * mm, "end": v(-80, 80) * mm});
            skArc(sketch, "E79.7", {"start": v(70, -90) * mm, "mid": v(77.07, -87.07) * mm, "end": v(80, -80) * mm});
            skLineSegment(sketch, "E79.8", {"start": v(-70, -90) * mm, "end": v(70, -90) * mm});
            skArc(sketch, "E79.9", {"start": v(-80, -80) * mm, "mid": v(-77.07, -87.07) * mm, "end": v(-70, -90) * mm});
            skCircle(sketch, "E79.10", {"center": v(-60, -67.5) * mm, "radius": 4 * mm});
            skCircle(sketch, "E79.11", {"center": v(60, -67.5) * mm, "radius": 4 * mm});
            skArc(sketch, "E79.12", {"start": v(-56.15, -48.18) * mm, "mid": v(0, -67.5) * mm, "end": v(56.15, -48.18) * mm});
            skArc(sketch, "E79.13", {"start": v(56.15, -48.18) * mm, "mid": v(58.99, -44.68) * mm, "end": v(60, -40.3) * mm});
            skLineSegment(sketch, "E79.14", {"start": v(60, 40.3) * mm, "end": v(60, -40.3) * mm});
            skArc(sketch, "E79.15", {"start": v(-60, -40.3) * mm, "mid": v(-58.99, -44.68) * mm, "end": v(-56.15, -48.18) * mm});
            skLineSegment(sketch, "E79.16", {"start": v(-60, 40.3) * mm, "end": v(-60, -40.3) * mm});
            skArc(sketch, "E79.17", {"start": v(-56.15, 48.18) * mm, "mid": v(-58.99, 44.68) * mm, "end": v(-60, 40.3) * mm});
            skArc(sketch, "E79.18", {"start": v(56.15, 48.18) * mm, "mid": v(0, 67.5) * mm, "end": v(-56.15, 48.18) * mm});
            skArc(sketch, "E79.19", {"start": v(60, 40.3) * mm, "mid": v(58.99, 44.68) * mm, "end": v(56.15, 48.18) * mm});
            skLineSegment(sketch, "E79.20", {"start": v(14, -2.5) * mm, "end": v(-8, -2.5) * mm});
            skLineSegment(sketch, "E80", {"start": v(-35.48, 90) * mm, "end": v(-17.48, 108) * mm});
            skLineSegment(sketch, "E81", {"start": v(30.52, 90) * mm, "end": v(12.52, 108) * mm});
            skLineSegment(sketch, "E82", {"start": v(-17.48, 108) * mm, "end": v(-17.48, 120) * mm});
            skLineSegment(sketch, "E83", {"start": v(12.52, 108) * mm, "end": v(12.52, 120) * mm});
            skArc(sketch, "E84", {"start": v(12.52, 120) * mm, "mid": v(-2.48, 135) * mm, "end": v(-17.48, 120) * mm});
            skCircle(sketch, "E85", {"center": v(-2.48, 120) * mm, "radius": 6 * mm});
            skLineSegment(sketch, "E86", {"start": v(-2.48, 120) * mm, "end": v(-2.48, 90) * mm, "construction": true});
            skLineSegment(sketch, "E87", {"start": v(-80, 0) * mm, "end": v(80, 0) * mm, "construction": true});
            skLineSegment(sketch, "E88.MirrorCS", {"start": v(30.52, -90) * mm, "end": v(12.52, -108) * mm});
            skLineSegment(sketch, "E89.MirrorCS", {"start": v(12.52, -108) * mm, "end": v(12.52, -120) * mm});
            skArc(sketch, "E90.MirrorCS", {"start": v(12.52, -120) * mm, "mid": v(-2.48, -135) * mm, "end": v(-17.48, -120) * mm});
            skLineSegment(sketch, "E91.MirrorCS", {"start": v(-17.48, -108) * mm, "end": v(-17.48, -120) * mm});
            skLineSegment(sketch, "E92.MirrorCS", {"start": v(-35.48, -90) * mm, "end": v(-17.48, -108) * mm});
            skCircle(sketch, "E93.MirrorC", {"center": v(-2.48, -120) * mm, "radius": 6 * mm});
            skLineSegment(sketch, "E94.MirrorCS", {"start": v(-2.48, -120) * mm, "end": v(-2.48, -90) * mm, "construction": true});
            skSolve(sketch);
        }
        {
            var Q0;
            {var subQ1=sQuery(id+"F16.wireOp",EDGE,"E80");Q0=makeQuery(id+"F16.imprint","IMPRINT",FACE,{"disambiguationData":[TD([[makeQuery(id+"F16.imprint","IMPRINT",EDGE,{"derivedFrom":subQ1}),-1.0]])]});}
            var Q1;
            {var subQ9=sQuery(id+"F16.wireOp",EDGE,"E79.0");Q1=makeQuery(id+"F16.imprint","IMPRINT",FACE,{"disambiguationData":[TD([[makeQuery(id+"F16.imprint","IMPRINT",EDGE,{"derivedFrom":subQ9}),1.0]])]});}
            var Q2;
            {var subQ0=sQuery(id+"F16.wireOp",EDGE,"E88.MirrorCS");Q2=makeQuery(id+"F16.imprint","IMPRINT",FACE,{"disambiguationData":[TD([[makeQuery(id+"F16.imprint","IMPRINT",EDGE,{"derivedFrom":subQ0}),-1.0]])]});}
            var Q3;
            Q3=makeQuery(id+"F2.opExtrude","CAP_FACE",FACE,{"disambiguationData":[OSD([sQuery(id+"F0.wireOp",EDGE,"E12"),sQuery(id+"F0.wireOp",EDGE,"E13"),sQuery(id+"F0.wireOp",EDGE,"E14"),sQuery(id+"F0.wireOp",EDGE,"E15"),sQuery(id+"F0.wireOp",EDGE,"E17.filletArc"),sQuery(id+"F0.wireOp",EDGE,"E18.filletArc"),sQuery(id+"F0.wireOp",EDGE,"E19.filletArc"),sQuery(id+"F0.wireOp",EDGE,"E20.filletArc"),sQuery(id+"F0.wireOp",EDGE,"E25.0"),sQuery(id+"F0.wireOp",EDGE,"E25.1"),sQuery(id+"F0.wireOp",EDGE,"E25.2"),sQuery(id+"F0.wireOp",EDGE,"E25.3"),sQuery(id+"F0.wireOp",EDGE,"E25.4"),sQuery(id+"F0.wireOp",EDGE,"E25.5"),sQuery(id+"F0.wireOp",EDGE,"E25.6"),sQuery(id+"F0.wireOp",EDGE,"E25.7")])],"isStart":false});
            extrude(context, id + "F17", {"entities" : qUnion([Q0, Q1, Q2]), "endBound" : BoundingType.UP_TO_SURFACE, "endBoundEntityFace" : qUnion([Q3]), "depth" : 25 * mm});
        }
    });
